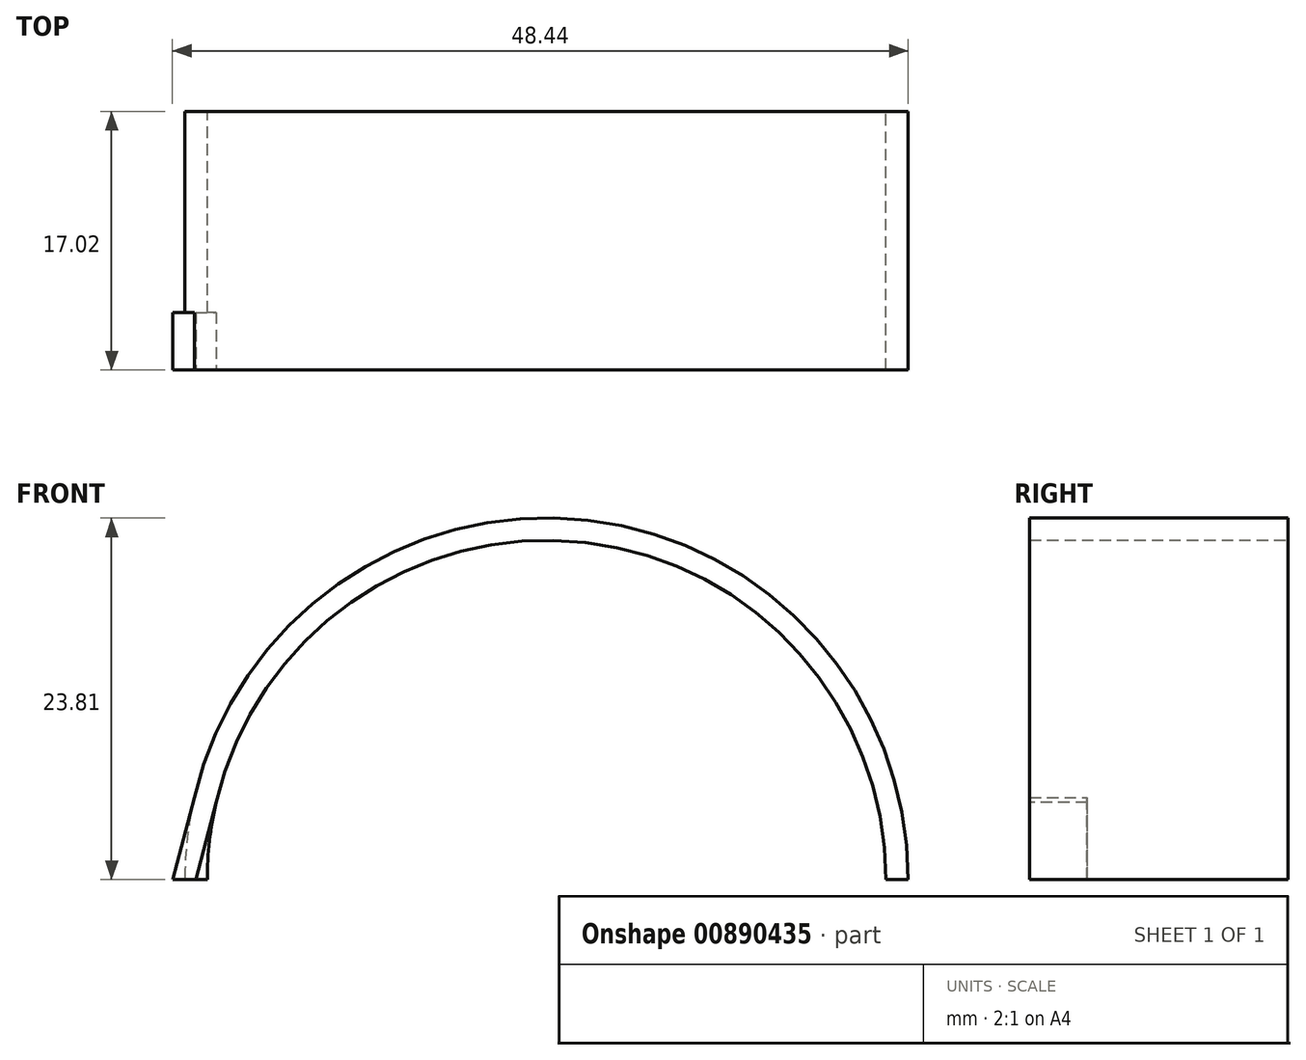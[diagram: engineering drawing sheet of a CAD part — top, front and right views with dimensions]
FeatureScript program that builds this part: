
annotation { "Feature Type Name" : "Feature", "Feature Type Description" : "" }
export const myFeature = defineFeature(function(context is Context, id is Id, definition is map)
    precondition{}
    {
        {
            var Q0;
            Q0=qCreatedBy(makeId("Front.planeOp"),FACE);
            var sketch = newSketch(context, id + "F0", { "sketchPlane" : qUnion([Q0])});
            skArc(sketch, "E0", {"start": v(22.34, 0) * mm, "mid": v(0, 22.34) * mm, "end": v(-22.34, 0) * mm});
            skArc(sketch, "E1", {"start": v(23.81, 0) * mm, "mid": v(0, 23.81) * mm, "end": v(-23.81, 0) * mm});
            skLineSegment(sketch, "E2", {"start": v(22.34, 0) * mm, "end": v(23.81, 0) * mm});
            skLineSegment(sketch, "E3", {"start": v(-23.81, 0) * mm, "end": v(-22.34, 0) * mm});
            skSolve(sketch);
        }
        {
            var Q0;
            Q0=makeQuery(id+"F0.imprint","IMPRINT",FACE,{"disambiguationData":[TD([[makeQuery(id+"F0.imprint","IMPRINT",EDGE,{"derivedFrom":sQuery(id+"F0.wireOp",EDGE,"E0")}),-1.0]])]});
            extrude(context, id + "F1", {"entities" : qUnion([Q0]), "endBound" : BoundingType.SYMMETRIC, "depth" : 17.02 * mm, "offsetDistance" : 25 * mm});
        }
        {
            var Q0;
            Q0=makeQuery(id+"F1.opExtrude","CAP_FACE",FACE,{"disambiguationData":[OSD([sQuery(id+"F0.wireOp",EDGE,"E0"),sQuery(id+"F0.wireOp",EDGE,"E1"),sQuery(id+"F0.wireOp",EDGE,"E2"),sQuery(id+"F0.wireOp",EDGE,"E3")])],"isStart":false});
            var sketch = newSketch(context, id + "F2", { "sketchPlane" : qUnion([Q0])});
            skArc(sketch, "E4", {"start": v(-22.34, 0) * mm, "mid": v(-22.2, 2.56) * mm, "end": v(-21.75, 5.08) * mm});
            skLineSegment(sketch, "E5", {"start": v(-26.22, 5.08) * mm, "end": v(-19.86, 5.08) * mm, "construction": true});
            skArc(sketch, "E6", {"start": v(-24.28, 0) * mm, "mid": v(-24.12, 2.8) * mm, "end": v(-23.63, 5.58) * mm});
            skLineSegment(sketch, "E7", {"start": v(-21.75, 5.08) * mm, "end": v(-23.64, 5.52) * mm});
            skLineSegment(sketch, "E8", {"start": v(-24.28, 0) * mm, "end": v(-22.34, 0) * mm});
            skSolve(sketch);
        }
        {
            var Q0;
            Q0 = qSketchRegion(id + "F2", true);
            extrude(context, id + "F3", {"entities" : qUnion([Q0]), "operationType" : NewBodyOperationType.REMOVE, "oppositeDirection" : true, "depth" : 3.78 * mm, "offsetDistance" : 25 * mm});
        }
        {
            var Q0;
            Q0=makeQuery(id+"F1.opExtrude","CAP_FACE",FACE,{"disambiguationData":[OSD([sQuery(id+"F0.wireOp",EDGE,"E0"),sQuery(id+"F0.wireOp",EDGE,"E1"),sQuery(id+"F0.wireOp",EDGE,"E2"),sQuery(id+"F0.wireOp",EDGE,"E3")])],"isStart":false});
            var sketch = newSketch(context, id + "F4", { "sketchPlane" : qUnion([Q0])});
            skLineSegment(sketch, "E9", {"start": v(-23.19, 5.42) * mm, "end": v(-24.63, 0) * mm});
            skLineSegment(sketch, "E10", {"start": v(-21.75, 5.08) * mm, "end": v(-23.1, 0) * mm});
            skLineSegment(sketch, "E11", {"start": v(-24.63, 0) * mm, "end": v(-23.1, 0) * mm});
            skLineSegment(sketch, "E12", {"start": v(-21.75, 5.08) * mm, "end": v(-23.19, 5.42) * mm});
            skSolve(sketch);
        }
        {
            var Q0;
            Q0=makeQuery(id+"F4.imprint","IMPRINT",FACE,{"disambiguationData":[TD([[makeQuery(id+"F4.imprint","IMPRINT",EDGE,{"derivedFrom":sQuery(id+"F4.wireOp",EDGE,"E9")}),1.0]])]});
            var Q1;
            Q1=makeQuery(id+"F3.boolean.opBoolean","COPY",FACE,{"derivedFrom":makeQuery(id+"F3.opExtrude","CAP_FACE",FACE,{"disambiguationData":[OSD([sQuery(id+"F2.wireOp",EDGE,"E4"),sQuery(id+"F2.wireOp",EDGE,"E6"),sQuery(id+"F2.wireOp",EDGE,"E7"),sQuery(id+"F2.wireOp",EDGE,"E8")])],"isStart":false})});
            extrude(context, id + "F5", {"entities" : qUnion([Q0]), "operationType" : NewBodyOperationType.ADD, "endBound" : BoundingType.UP_TO_SURFACE, "oppositeDirection" : true, "depth" : 25 * mm, "endBoundEntityFace" : qUnion([Q1]), "offsetDistance" : 25 * mm});
        }
    });
